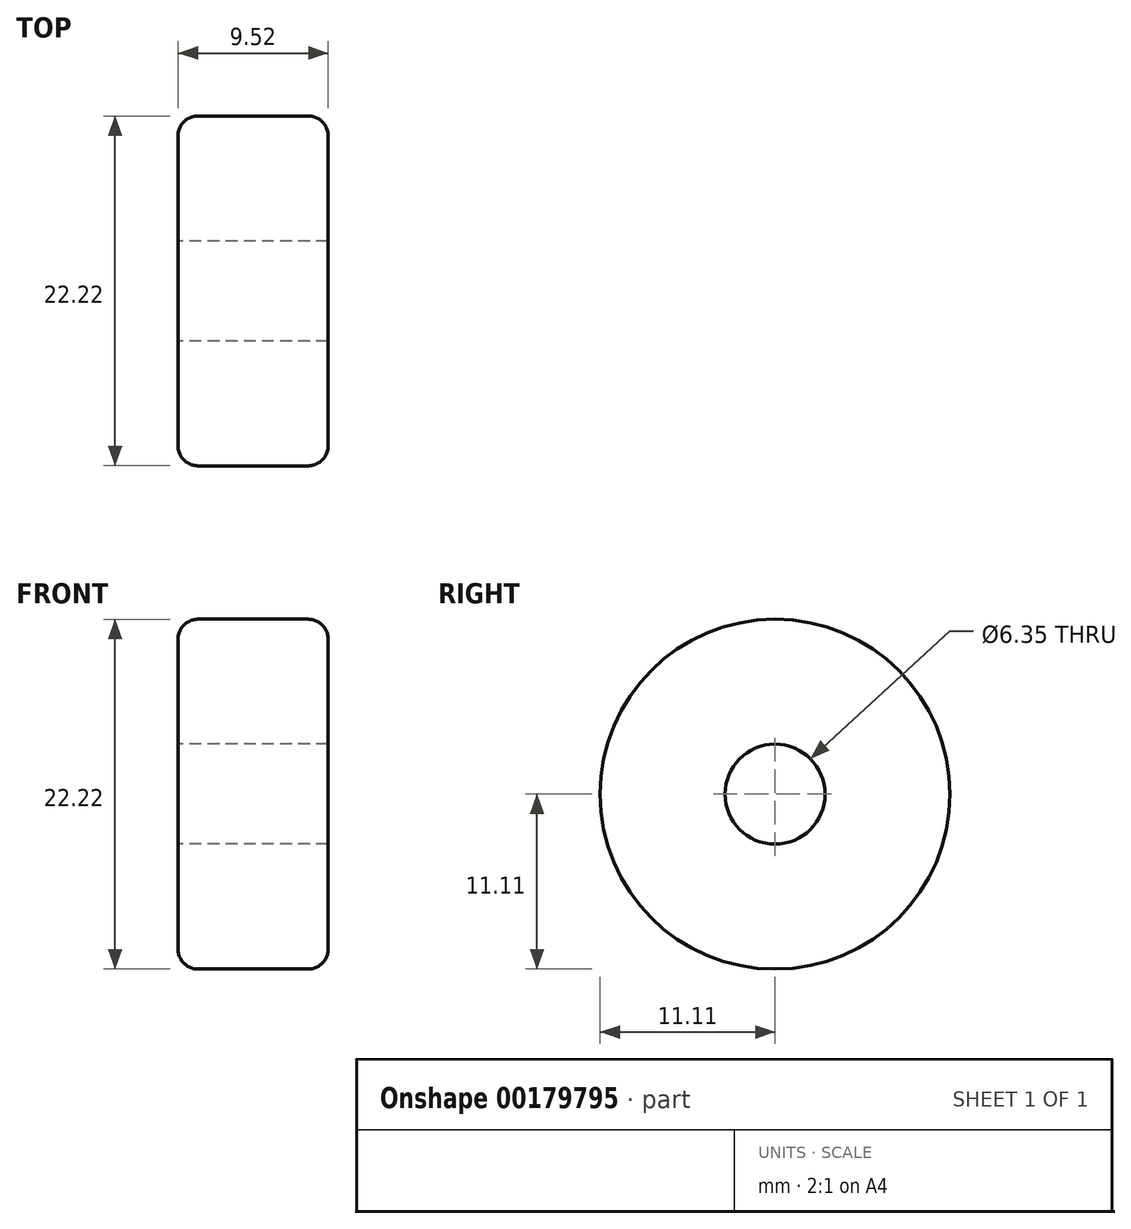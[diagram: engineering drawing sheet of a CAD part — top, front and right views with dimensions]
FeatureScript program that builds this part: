
annotation { "Feature Type Name" : "Feature", "Feature Type Description" : "" }
export const myFeature = defineFeature(function(context is Context, id is Id, definition is map)
    precondition{}
    {
        {
            var Q0;
            Q0=qCreatedBy(makeId("Right.planeOp"),FACE);
            var sketch = newSketch(context, id + "F0", { "sketchPlane" : qUnion([Q0])});
            skCircle(sketch, "E0", {"center": v(0, 0) * mm, "radius": 3.18 * mm});
            skCircle(sketch, "E1", {"center": v(0, 0) * mm, "radius": 11.11 * mm});
            skSolve(sketch);
        }
        {
            var Q0;
            Q0 = qSketchRegion(id + "F0", true);
            extrude(context, id + "F1", {"entities" : qUnion([Q0]), "endBound" : BoundingType.SYMMETRIC, "depth" : 9.52 * mm});
        }
        {
            var Q0;
            Q0=makeQuery(id+"F1.opExtrude","CAP_EDGE",EDGE,{"disambiguationData":[OSD([sQuery(id+"F0.wireOp",EDGE,"E1")])],"isStart":false});
            var Q1;
            Q1=makeQuery(id+"F1.opExtrude","CAP_EDGE",EDGE,{"disambiguationData":[OSD([sQuery(id+"F0.wireOp",EDGE,"E1")])],"isStart":true});
            fillet(context, id + "F2", {"entities" : qUnion([Q0, Q1]), "radius" : 1.27 * mm, "tangentPropagation" : true, "allowEdgeOverflow" : false});
        }
    });
